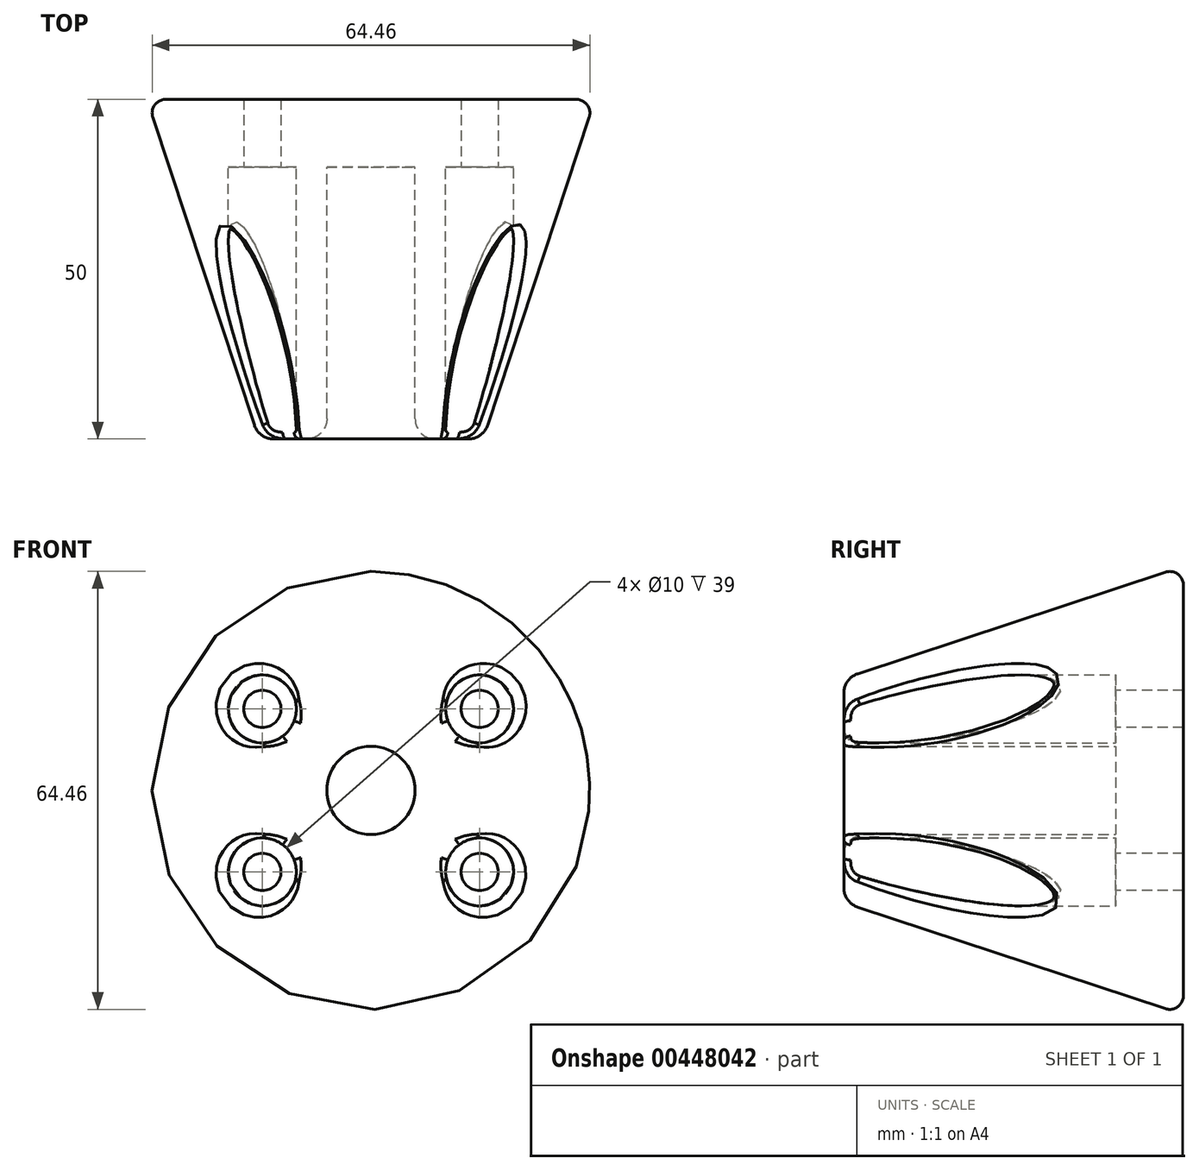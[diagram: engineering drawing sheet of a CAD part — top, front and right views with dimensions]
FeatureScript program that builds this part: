
annotation { "Feature Type Name" : "Feature", "Feature Type Description" : "" }
export const myFeature = defineFeature(function(context is Context, id is Id, definition is map)
    precondition{}
    {
        {
            var Q0;
            Q0=qCreatedBy(makeId("Right.planeOp"),FACE);
            var sketch = newSketch(context, id + "F0", { "sketchPlane" : qUnion([Q0])});
            skLineSegment(sketch, "E0", {"start": v(10, 0) * mm, "end": v(10, 33) * mm});
            skLineSegment(sketch, "E1", {"start": v(10, 33) * mm, "end": v(-40, 16.5) * mm});
            skLineSegment(sketch, "E2", {"start": v(-40, 6.5) * mm, "end": v(0, 6.5) * mm});
            skLineSegment(sketch, "E3", {"start": v(-40, 16.5) * mm, "end": v(-40, 6.5) * mm});
            skLineSegment(sketch, "E4", {"start": v(10, 0) * mm, "end": v(0, 0) * mm});
            skLineSegment(sketch, "E5", {"start": v(0, 0) * mm, "end": v(0, 6.5) * mm});
            skSolve(sketch);
        }
        {
            var Q0;
            Q0=makeQuery(id+"F0.imprint","IMPRINT",FACE,{"disambiguationData":[TD([[makeQuery(id+"F0.imprint","IMPRINT",EDGE,{"derivedFrom":sQuery(id+"F0.wireOp",EDGE,"E0")}),1.0]])]});
            var Q1;
            Q1=sQuery(id+"F0.wireOp",EDGE,"E4");
            revolve(context, id + "F1", {"entities" : qUnion([Q0]), "axis" : qUnion([Q1]), "revolveType" : RevolveType.FULL});
        }
        {
            var Q0;
            Q0=qCreatedBy(makeId("Front.planeOp"),FACE);
            var sketch = newSketch(context, id + "F2", { "sketchPlane" : qUnion([Q0])});
            skLineSegment(sketch, "E6.bottom", {"start": v(16, 12) * mm, "end": v(-16, 12) * mm, "construction": true});
            skLineSegment(sketch, "E6.top", {"start": v(16, -12) * mm, "end": v(-16, -12) * mm, "construction": true});
            skLineSegment(sketch, "E6.left", {"start": v(16, 12) * mm, "end": v(16, -12) * mm, "construction": true});
            skLineSegment(sketch, "E6.right", {"start": v(-16, 12) * mm, "end": v(-16, -12) * mm, "construction": true});
            skPoint(sketch, "E6.middle", {"position": v(0, 0) * mm});
            skCircle(sketch, "E7", {"center": v(-16, 12) * mm, "radius": 2.75 * mm});
            skCircle(sketch, "E8", {"center": v(-16, -12) * mm, "radius": 2.75 * mm});
            skCircle(sketch, "E9", {"center": v(16, -12) * mm, "radius": 2.75 * mm});
            skCircle(sketch, "E10", {"center": v(16, 12) * mm, "radius": 2.75 * mm});
            skCircle(sketch, "E11", {"center": v(16, 12) * mm, "radius": 5 * mm});
            skCircle(sketch, "E12", {"center": v(16, -12) * mm, "radius": 5 * mm});
            skCircle(sketch, "E13", {"center": v(-16, -12) * mm, "radius": 5 * mm});
            skCircle(sketch, "E14", {"center": v(-16, 12) * mm, "radius": 5 * mm});
            skSolve(sketch);
        }
        {
            var Q0;
            Q0=makeQuery(id+"F2.imprint","IMPRINT",FACE,{"disambiguationData":[TD([[makeQuery(id+"F2.imprint","IMPRINT",EDGE,{"derivedFrom":sQuery(id+"F2.wireOp",EDGE,"E10")}),1.0]])]});
            var Q1;
            Q1=makeQuery(id+"F2.imprint","IMPRINT",FACE,{"disambiguationData":[TD([[makeQuery(id+"F2.imprint","IMPRINT",EDGE,{"derivedFrom":sQuery(id+"F2.wireOp",EDGE,"E7")}),1.0]])]});
            var Q2;
            Q2=makeQuery(id+"F2.imprint","IMPRINT",FACE,{"disambiguationData":[TD([[makeQuery(id+"F2.imprint","IMPRINT",EDGE,{"derivedFrom":sQuery(id+"F2.wireOp",EDGE,"E8")}),1.0]])]});
            var Q3;
            Q3=makeQuery(id+"F2.imprint","IMPRINT",FACE,{"disambiguationData":[TD([[makeQuery(id+"F2.imprint","IMPRINT",EDGE,{"derivedFrom":sQuery(id+"F2.wireOp",EDGE,"E9")}),1.0]])]});
            var Q4;
            Q4=makeQuery(id+"F1.opRevolve","SWEPT_FACE",FACE,{"disambiguationData":[OSD([sQuery(id+"F0.wireOp",EDGE,"E0")])]});
            extrude(context, id + "F3", {"entities" : qUnion([Q0, Q1, Q2, Q3]), "operationType" : NewBodyOperationType.REMOVE, "endBound" : BoundingType.UP_TO_SURFACE, "oppositeDirection" : true, "endBoundEntityFace" : qUnion([Q4]), "depth" : 25 * mm});
        }
        {
            var Q0;
            Q0=makeQuery(id+"F2.imprint","IMPRINT",FACE,{"disambiguationData":[TD([[makeQuery(id+"F2.imprint","IMPRINT",EDGE,{"derivedFrom":sQuery(id+"F2.wireOp",EDGE,"E10")}),-1.0]])]});
            var Q1;
            Q1=makeQuery(id+"F2.imprint","IMPRINT",FACE,{"disambiguationData":[TD([[makeQuery(id+"F2.imprint","IMPRINT",EDGE,{"derivedFrom":sQuery(id+"F2.wireOp",EDGE,"E7")}),-1.0]])]});
            var Q2;
            Q2=makeQuery(id+"F2.imprint","IMPRINT",FACE,{"disambiguationData":[TD([[makeQuery(id+"F2.imprint","IMPRINT",EDGE,{"derivedFrom":sQuery(id+"F2.wireOp",EDGE,"E8")}),-1.0]])]});
            var Q3;
            Q3=makeQuery(id+"F2.imprint","IMPRINT",FACE,{"disambiguationData":[TD([[makeQuery(id+"F2.imprint","IMPRINT",EDGE,{"derivedFrom":sQuery(id+"F2.wireOp",EDGE,"E9")}),-1.0]])]});
            var Q4;
            Q4=makeQuery(id+"F2.imprint","IMPRINT",FACE,{"disambiguationData":[TD([[makeQuery(id+"F2.imprint","IMPRINT",EDGE,{"derivedFrom":sQuery(id+"F2.wireOp",EDGE,"E10")}),1.0]])]});
            var Q5;
            Q5=makeQuery(id+"F2.imprint","IMPRINT",FACE,{"disambiguationData":[TD([[makeQuery(id+"F2.imprint","IMPRINT",EDGE,{"derivedFrom":sQuery(id+"F2.wireOp",EDGE,"E7")}),1.0]])]});
            var Q6;
            Q6=makeQuery(id+"F2.imprint","IMPRINT",FACE,{"disambiguationData":[TD([[makeQuery(id+"F2.imprint","IMPRINT",EDGE,{"derivedFrom":sQuery(id+"F2.wireOp",EDGE,"E8")}),1.0]])]});
            var Q7;
            Q7=makeQuery(id+"F2.imprint","IMPRINT",FACE,{"disambiguationData":[TD([[makeQuery(id+"F2.imprint","IMPRINT",EDGE,{"derivedFrom":sQuery(id+"F2.wireOp",EDGE,"E9")}),1.0]])]});
            extrude(context, id + "F4", {"entities" : qUnion([Q0, Q1, Q2, Q3, Q4, Q5, Q6, Q7]), "operationType" : NewBodyOperationType.REMOVE, "endBound" : BoundingType.THROUGH_ALL, "depth" : 25 * mm});
        }
        {
            var Q0;
            Q0=makeQuery(id+"F1.opRevolve","SWEPT_EDGE",EDGE,{"disambiguationData":[OSD([sQuery(id+"F0.wireOp",EDGE,"E2"),sQuery(id+"F0.wireOp",EDGE,"E3")])]});
            var Q1;
            Q1=makeQuery(id+"F1.opRevolve","SWEPT_EDGE",EDGE,{"disambiguationData":[OSD([sQuery(id+"F0.wireOp",EDGE,"E1"),sQuery(id+"F0.wireOp",EDGE,"E3")])]});
            fillet(context, id + "F5", {"entities" : qUnion([Q0, Q1]), "radius" : 3 * mm, "tangentPropagation" : true, "allowEdgeOverflow" : false});
        }
        {
            var Q0;
            Q0=makeQuery(id+"F4.boolean.opBoolean","INTERSECT",EDGE,{"derivedFrom":[makeQuery(id+"F1.opRevolve","SWEPT_FACE",FACE,{"disambiguationData":[OSD([sQuery(id+"F0.wireOp",EDGE,"E1")])]}),makeQuery(id+"F4.opExtrude","SWEPT_FACE",FACE,{"disambiguationData":[OSD([sQuery(id+"F2.wireOp",EDGE,"E13")])]})]});
            var Q1;
            Q1=makeQuery(id+"F4.boolean.opBoolean","INTERSECT",EDGE,{"derivedFrom":[makeQuery(id+"F1.opRevolve","SWEPT_FACE",FACE,{"disambiguationData":[OSD([sQuery(id+"F0.wireOp",EDGE,"E1")])]}),makeQuery(id+"F4.opExtrude","SWEPT_FACE",FACE,{"disambiguationData":[OSD([sQuery(id+"F2.wireOp",EDGE,"E12")])]})]});
            var Q2;
            Q2=makeQuery(id+"F4.boolean.opBoolean","INTERSECT",EDGE,{"derivedFrom":[makeQuery(id+"F1.opRevolve","SWEPT_FACE",FACE,{"disambiguationData":[OSD([sQuery(id+"F0.wireOp",EDGE,"E1")])]}),makeQuery(id+"F4.opExtrude","SWEPT_FACE",FACE,{"disambiguationData":[OSD([sQuery(id+"F2.wireOp",EDGE,"E11")])]})]});
            var Q3;
            Q3=makeQuery(id+"F4.boolean.opBoolean","INTERSECT",EDGE,{"derivedFrom":[makeQuery(id+"F1.opRevolve","SWEPT_FACE",FACE,{"disambiguationData":[OSD([sQuery(id+"F0.wireOp",EDGE,"E1")])]}),makeQuery(id+"F4.opExtrude","SWEPT_FACE",FACE,{"disambiguationData":[OSD([sQuery(id+"F2.wireOp",EDGE,"E14")])]})]});
            fillet(context, id + "F6", {"entities" : qUnion([Q0, Q1, Q2, Q3]), "radius" : 1 * mm, "tangentPropagation" : true, "allowEdgeOverflow" : false});
        }
        {
            var Q0;
            Q0=makeQuery(id+"F1.opRevolve","SWEPT_EDGE",EDGE,{"disambiguationData":[OSD([sQuery(id+"F0.wireOp",EDGE,"E0"),sQuery(id+"F0.wireOp",EDGE,"E1")])]});
            fillet(context, id + "F7", {"entities" : qUnion([Q0]), "radius" : 2 * mm, "tangentPropagation" : true, "allowEdgeOverflow" : false});
        }
    });
